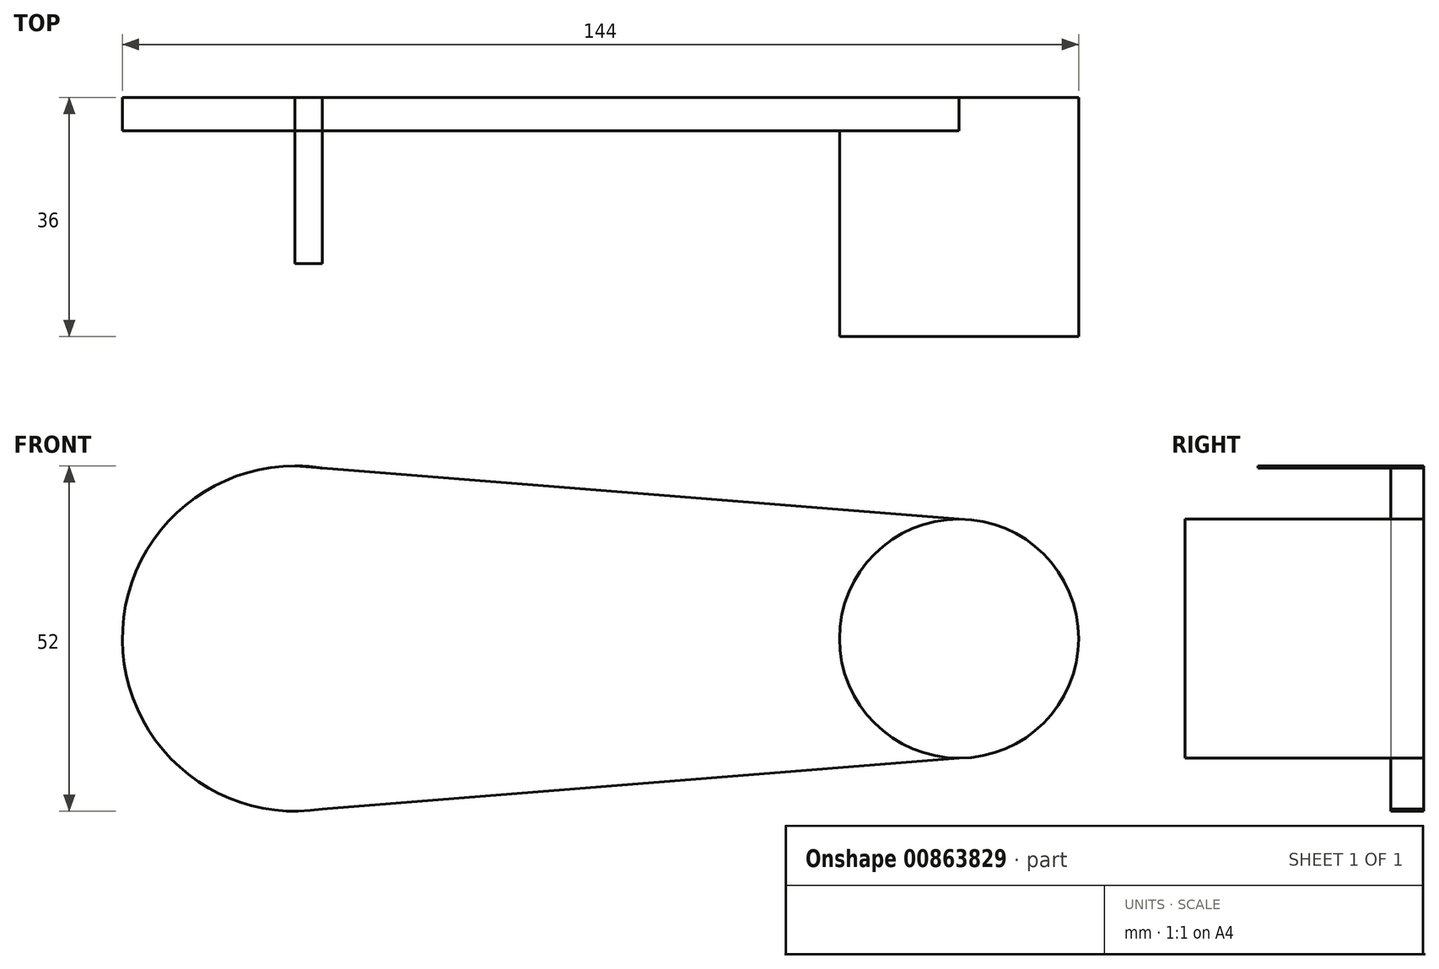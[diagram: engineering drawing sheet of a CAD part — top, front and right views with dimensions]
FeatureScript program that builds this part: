
annotation { "Feature Type Name" : "Feature", "Feature Type Description" : "" }
export const myFeature = defineFeature(function(context is Context, id is Id, definition is map)
    precondition{}
    {
        {
            var Q0;
            Q0=qCreatedBy(makeId("Front.planeOp"),FACE);
            var sketch = newSketch(context, id + "F0", { "sketchPlane" : qUnion([Q0])});
            skCircle(sketch, "E0", {"center": v(-58.83, 0) * mm, "radius": 26 * mm});
            skCircle(sketch, "E1", {"center": v(41.17, 0) * mm, "radius": 18 * mm});
            skLineSegment(sketch, "E2", {"start": v(-58.83, 26) * mm, "end": v(41.17, 18) * mm});
            skLineSegment(sketch, "E3", {"start": v(41.17, -18) * mm, "end": v(-58.83, -26) * mm});
            skSolve(sketch);
        }
        {
            var Q0;
            {var subQ0=sQuery(id+"F0.wireOp",EDGE,"E2");var subQ1=sQuery(id+"F0.wireOp",EDGE,"E0");var subQ2=makeQuery(id+"F0.imprint","INTERSECT",VERTEX,{"disambiguationData":[OD(0.0)],"derivedFrom":[subQ1,subQ0]});Q0=makeQuery(id+"F0.imprint","IMPRINT",FACE,{"disambiguationData":[TD([[makeQuery(id+"F0.imprint","IMPRINT",EDGE,{"disambiguationData":[TD([[subQ2,-1.0]])],"derivedFrom":subQ1}),1.0]])]});}
            extrude(context, id + "F1", {"entities" : qUnion([Q0]), "depth" : 25 * mm, "offsetDistance" : 25 * mm});
        }
        {
            var Q0;
            Q0 = qSketchRegion(id + "F0", true);
            extrude(context, id + "F2", {"entities" : qUnion([Q0]), "depth" : 5 * mm, "offsetDistance" : 25 * mm});
        }
        {
            var Q0;
            {var subQ0=sQuery(id+"F0.wireOp",EDGE,"E1");var subQ1=makeQuery(id+"F0.imprint","INTERSECT",VERTEX,{"derivedFrom":[subQ0,sQuery(id+"F0.wireOp",EDGE,"E2")]});Q0=makeQuery(id+"F0.imprint","IMPRINT",FACE,{"disambiguationData":[TD([[makeQuery(id+"F0.imprint","IMPRINT",EDGE,{"disambiguationData":[TD([[subQ1,-1.0]])],"derivedFrom":subQ0}),1.0]])]});}
            extrude(context, id + "F3", {"entities" : qUnion([Q0]), "operationType" : NewBodyOperationType.ADD, "depth" : 36 * mm, "offsetDistance" : 25 * mm});
        }
    });
